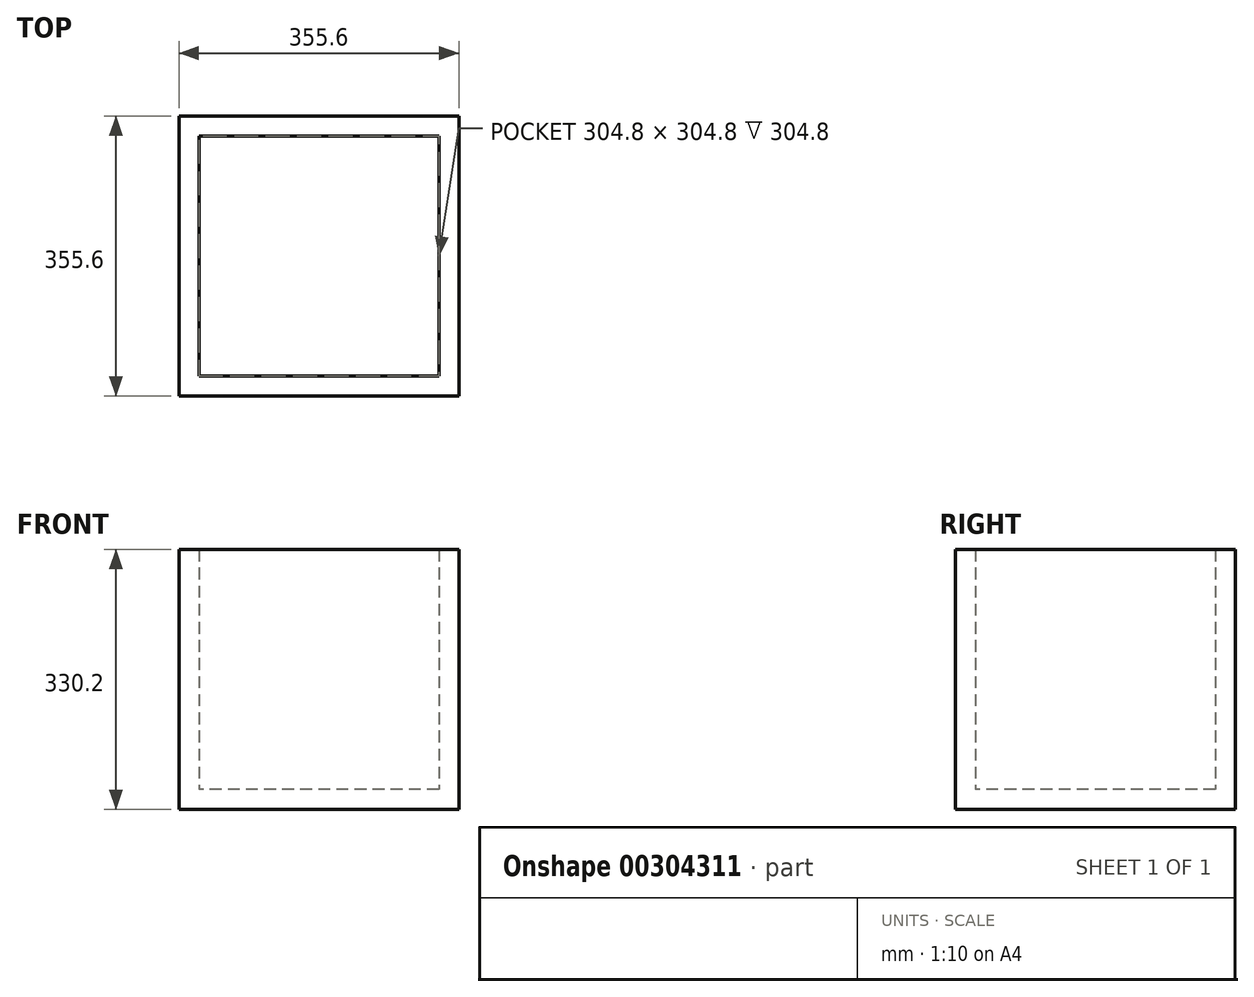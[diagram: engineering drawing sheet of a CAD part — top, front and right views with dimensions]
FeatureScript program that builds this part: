
annotation { "Feature Type Name" : "Feature", "Feature Type Description" : "" }
export const myFeature = defineFeature(function(context is Context, id is Id, definition is map)
    precondition{}
    {
        {
            var Q0;
            Q0=qCreatedBy(makeId("Top.planeOp"),FACE);
            var sketch = newSketch(context, id + "F0", { "sketchPlane" : qUnion([Q0])});
            skLineSegment(sketch, "E0.bottom", {"start": v(152.4, 152.4) * mm, "end": v(-152.4, 152.4) * mm});
            skLineSegment(sketch, "E0.top", {"start": v(152.4, -152.4) * mm, "end": v(-152.4, -152.4) * mm});
            skLineSegment(sketch, "E0.left", {"start": v(152.4, 152.4) * mm, "end": v(152.4, -152.4) * mm});
            skLineSegment(sketch, "E0.right", {"start": v(-152.4, 152.4) * mm, "end": v(-152.4, -152.4) * mm});
            skPoint(sketch, "E0.middle", {"position": v(0, 0) * mm});
            skSolve(sketch);
        }
        {
            var Q0;
            Q0 = qSketchRegion(id + "F0", true);
            extrude(context, id + "F1", {"entities" : qUnion([Q0]), "depth" : 25.4 * mm});
        }
        {
            var Q0;
            Q0=makeQuery(id+"F1.opExtrude","SWEPT_FACE",FACE,{"disambiguationData":[OSD([sQuery(id+"F0.wireOp",EDGE,"E0.top")])]});
            var sketch = newSketch(context, id + "F2", { "sketchPlane" : qUnion([Q0])});
            skLineSegment(sketch, "E1.bottom", {"start": v(-152.4, 0) * mm, "end": v(152.4, 0) * mm});
            skLineSegment(sketch, "E1.top", {"start": v(-152.4, 330.2) * mm, "end": v(152.4, 330.2) * mm});
            skLineSegment(sketch, "E1.left", {"start": v(-152.4, 0) * mm, "end": v(-152.4, 330.2) * mm});
            skLineSegment(sketch, "E1.right", {"start": v(152.4, 0) * mm, "end": v(152.4, 330.2) * mm});
            skSolve(sketch);
        }
        {
            var Q0;
            Q0 = qSketchRegion(id + "F2", true);
            extrude(context, id + "F3", {"entities" : qUnion([Q0]), "operationType" : NewBodyOperationType.ADD, "depth" : 25.4 * mm});
        }
        {
            var Q0;
            Q0=makeQuery(id+"F1.opExtrude","SWEPT_BODY",BODY,{"disambiguationData":[OSD([sQuery(id+"F0.wireOp",EDGE,"E0.bottom"),sQuery(id+"F0.wireOp",EDGE,"E0.top"),sQuery(id+"F0.wireOp",EDGE,"E0.left"),sQuery(id+"F0.wireOp",EDGE,"E0.right")])]});
            var Q1;
            Q1=qCreatedBy(makeId("Front.planeOp"),FACE);
            mirror(context, id + "F4", {"operationType" : NewBodyOperationType.ADD, "entities" : qUnion([Q0]), "mirrorPlane" : qUnion([Q1])});
        }
        {
            var Q0;
            {var subQ0=makeQuery(id+"F3.boolean.opBoolean","MERGE",FACE,{"derivedFrom":[makeQuery(id+"F1.opExtrude","SWEPT_FACE",FACE,{"disambiguationData":[OSD([sQuery(id+"F0.wireOp",EDGE,"E0.left")])]}),makeQuery(id+"F3.opExtrude","SWEPT_FACE",FACE,{"disambiguationData":[OSD([sQuery(id+"F2.wireOp",EDGE,"E1.right")])]})]});Q0=makeQuery(id+"F4.boolean.opBoolean","MERGE",FACE,{"derivedFrom":[subQ0,makeQuery(id+"F4.opPattern","COPY",FACE,{"derivedFrom":subQ0,"instanceName":"1"})]});}
            var sketch = newSketch(context, id + "F5", { "sketchPlane" : qUnion([Q0])});
            skLineSegment(sketch, "E2.bottom", {"start": v(-177.8, 0) * mm, "end": v(177.8, 0) * mm});
            skLineSegment(sketch, "E2.top", {"start": v(-177.8, 330.2) * mm, "end": v(177.8, 330.2) * mm});
            skLineSegment(sketch, "E2.left", {"start": v(-177.8, 0) * mm, "end": v(-177.8, 330.2) * mm});
            skLineSegment(sketch, "E2.right", {"start": v(177.8, 0) * mm, "end": v(177.8, 330.2) * mm});
            skSolve(sketch);
        }
        {
            var Q0;
            Q0 = qSketchRegion(id + "F5", true);
            extrude(context, id + "F6", {"entities" : qUnion([Q0]), "operationType" : NewBodyOperationType.ADD, "depth" : 25.4 * mm});
        }
        {
            var Q0;
            {var subQ0=makeQuery(id+"F3.boolean.opBoolean","MERGE",FACE,{"derivedFrom":[makeQuery(id+"F1.opExtrude","SWEPT_FACE",FACE,{"disambiguationData":[OSD([sQuery(id+"F0.wireOp",EDGE,"E0.right")])]}),makeQuery(id+"F3.opExtrude","SWEPT_FACE",FACE,{"disambiguationData":[OSD([sQuery(id+"F2.wireOp",EDGE,"E1.left")])]})]});Q0=makeQuery(id+"F4.boolean.opBoolean","MERGE",FACE,{"derivedFrom":[subQ0,makeQuery(id+"F4.opPattern","COPY",FACE,{"derivedFrom":subQ0,"instanceName":"1"})]});}
            var sketch = newSketch(context, id + "F7", { "sketchPlane" : qUnion([Q0])});
            skLineSegment(sketch, "E3.bottom", {"start": v(-177.8, 0) * mm, "end": v(177.8, 0) * mm});
            skLineSegment(sketch, "E3.top", {"start": v(-177.8, 330.2) * mm, "end": v(177.8, 330.2) * mm});
            skLineSegment(sketch, "E3.left", {"start": v(-177.8, 0) * mm, "end": v(-177.8, 330.2) * mm});
            skLineSegment(sketch, "E3.right", {"start": v(177.8, 0) * mm, "end": v(177.8, 330.2) * mm});
            skSolve(sketch);
        }
        {
            var Q0;
            Q0 = qSketchRegion(id + "F7", true);
            extrude(context, id + "F8", {"entities" : qUnion([Q0]), "operationType" : NewBodyOperationType.ADD, "depth" : 25.4 * mm});
        }
    });
